# Revit family: Albardilla MB escuadra EXT. C-1
name_source: partatom
category: Modelos genéricos
units: mm (PartAtom-declared; Revit-internal decimal feet)

## family parameters
Compartido = No
Corte con vacíos al cargar = No
Cota de conector redondo = Diámetro de uso
Puede alojar armadura = No
Punto de cálculo de habitación = No
Se basa en plano de trabajo = No
Siempre vertical = No
Tipo de pieza = Normal

## types (10) — shared parameters
Ancho escuadra = 500 mm
Descripción = Pieza de hormigón polímero con anclajes de acero inoxidable
Fabricante = ULMA Architectural Solutions
Material = Hormigón polímero STONEO. Color C-1
URL = https://www.ulmaarchitectural.com
zero-valued in all types: Elevación por defecto

## per-type parameters (varying)
| type | Ancho | Ancho dos | Ancho dos dist. | Ancho total | Anclajes | Dist. primer anclaje +30 | Modelo | Visible dos líneas | Visible una linea |
| MB12EE | 120 mm  [stored 0.393701 ft] | 85 mm  [stored 0.278871 ft] | 43 mm | 170 mm  [stored 0.557743 ft] | 85 mm  [stored 0.278871 ft] | 138 mm  [stored 0.452756 ft] | Albardilla MB12 en escuadra exterior | No | Sí |
| MB14EE | 140 mm  [stored 0.459318 ft] | 95 mm | 48 mm | 190 mm | 95 mm | 136 mm | Albardilla MB14 en escuadra exterior | No | Sí |
| MB17EE | 170 mm  [stored 0.557743 ft] | 110 mm  [stored 0.360892 ft] | 55 mm  [stored 0.180446 ft] | 220 mm  [stored 0.721785 ft] | 110 mm  [stored 0.360892 ft] | 133 mm  [stored 0.436352 ft] | Albardilla MB17 en escuadra exterior | No | Sí |
| MB19EE | 190 mm | 120 mm  [stored 0.393701 ft] | 60 mm  [stored 0.19685 ft] | 240 mm  [stored 0.787402 ft] | 120 mm  [stored 0.393701 ft] | 131 mm  [stored 0.42979 ft] | Albardilla MB19 en escuadra exterior | No | Sí |
| MB22EE | 220 mm  [stored 0.721785 ft] | 135 mm  [stored 0.442913 ft] | 68 mm | 270 mm  [stored 0.885827 ft] | 135 mm  [stored 0.442913 ft] | 128 mm  [stored 0.419948 ft] | Albardilla MB22 en escuadra exterior | No | Sí |
| MB25EE | 250 mm  [stored 0.82021 ft] | 150 mm | 75 mm | 300 mm | 150 mm | 125 mm  [stored 0.410105 ft] | Albardilla MB25 en escuadra exterior | No | Sí |
| MB30EE | 300 mm | 175 mm  [stored 0.574147 ft] | 88 mm | 350 mm  [stored 1.14829 ft] | 175 mm  [stored 0.574147 ft] | 120 mm  [stored 0.393701 ft] | Albardilla MB30 en escuadra exterior | Sí | No |
| MB35EE | 350 mm  [stored 1.14829 ft] | 200 mm  [stored 0.656168 ft] | 100 mm  [stored 0.328084 ft] | 400 mm  [stored 1.31234 ft] | 200 mm  [stored 0.656168 ft] | 115 mm  [stored 0.377297 ft] | Albardilla MB35 en escuadra exterior | Sí | No |
| MB40EE | 400 mm  [stored 1.31234 ft] | 225 mm  [stored 0.738189 ft] | 113 mm | 450 mm | 225 mm  [stored 0.738189 ft] | 110 mm  [stored 0.360892 ft] | Albardilla MB40 en escuadra exterior | Sí | No |
| MB27EE | 270 mm  [stored 0.885827 ft] | 160 mm  [stored 0.524934 ft] | 80 mm  [stored 0.262467 ft] | 320 mm  [stored 1.04987 ft] | 160 mm  [stored 0.524934 ft] | 123 mm  [stored 0.403543 ft] | Albardilla MB27 en escuadra exterior | No | Sí |

note: column(s) folded — value = type name in every type: Código de montaje

note: [stored X ft] marks values corroborated as IEEE doubles in the binary element streams (Revit-internal decimal feet)
